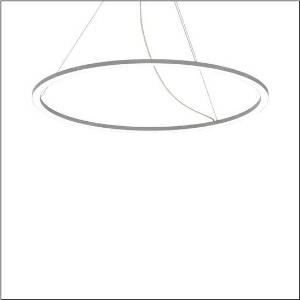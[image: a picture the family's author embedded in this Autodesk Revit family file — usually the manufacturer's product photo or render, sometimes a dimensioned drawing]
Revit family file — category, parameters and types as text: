
# Revit family: silica_r__21_ring-d_5pjbd4d1204a_bd2d
name_source: partatom
category: Lighting Fixtures
units: mm (PartAtom-declared; Revit-internal decimal feet)

## family parameters
Cut with Voids When Loaded = No
Host = Face
Light Source = No
Part Type = Normal
Room Calculation Point = No
Round Connector Dimension = Use Diameter
Shared = No

## types (1)
- Silica® 21 Ring-D (1 x LED, 10840 lm, 125 W, 3000K)
    Apparent Load = 125 VA
    CIE Flux Codes = 37 69 92 100 100
    Color Rendering = 80
    Color Temperature = 3000K
    Default Elevation = 1800 mm
    Description = Silica® 21 Ring-D, suspended luminaire, of PMMA, frosted, light emission: ring underside luminous distribution, primary light characteristic: symmetric, installation type: suspended mounting, LED, rated luminous flux: 10.840lm, luminous efficacy: 87lm/W, light colour: 830, colour temperature: 3000K, control gear: DALI 2, with terminal, 5-pole, mains connection: 230V, AC/DC, 0/50..60Hz, rated input power: 125W, housing, of extruded aluminium section, metallic grey (RAL 9006), diameter: 1.450mm, ceiling canopy, metallic grey (RAL 9006), protection rating (lamp compartment): IP40, insulation class (complete): insulation class I (protective earthing), certification: CE, impact resistance: IK02, permissible operating ambient temperature: 0..+35°C, packaging unit: 1 piece
    Height = 25 mm  [stored 0.082021 ft]
    Lamp = 1 x LED
    Lamp Light Flux = 10840 lm
    Lamp Power = 125 W
    Lamp count = 1
    Length = 1450 mm
    Luminous efficacy = 87 lm/W
    Manufacturer = Siteco
    ModVariant = No
    Model = 5PJBD4D1204A
    Mounting Place = Ceiling
    Mounting Type = Pendant
    Number of Poles = 1
    OnlyDefault = Yes
    Power Factor = 1
    Product Name = Silica® 21 Ring-D
    Product group = suspended luminaire
    ProductGroupID = 905
    Protection Class = Protection class I
    Protection Degree = IP 40
    RLX_Detail_Level = 1
    RLX_Emergency_Light_Flux = 0 lm
    RLX_Emergency_Type = 0
    RLX_Emergency_Type_DB = No
    RlxData = <blob elided: 17953 chars, md5=8f27d721>
    Socket = socket
    Standby Power = 0 W
    System Light Flux = 10840 lm
    System Power = 125 W
    Type Comments = Product without accessories
    Type Image = l_1251748.jpg
    URL = http://relux.com
    VarID = ---
    Voltage = 0 V
    Weight = 0.00 kg
    Width = 0 mm  [stored 0 ft]

note: [stored X ft] marks values corroborated as IEEE doubles in the binary element streams (Revit-internal decimal feet)

## geometry (parser evidence)
native form markers: Blend x4, Sweep x13
no freeform markers — native parametric forms only
